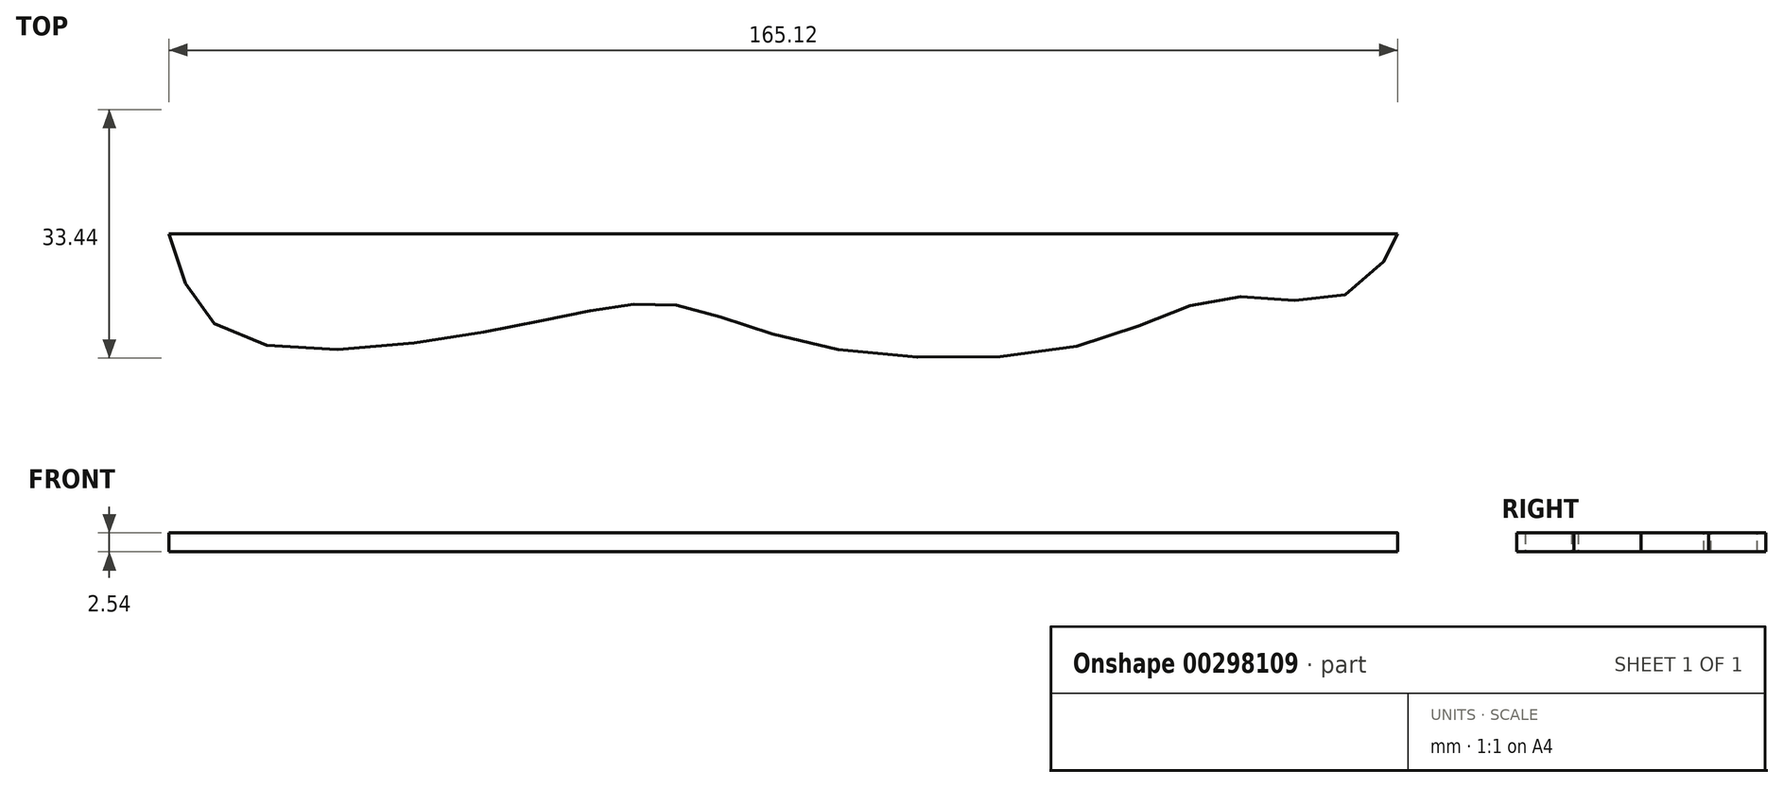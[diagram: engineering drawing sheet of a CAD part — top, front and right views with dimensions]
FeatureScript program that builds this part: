
annotation { "Feature Type Name" : "Feature", "Feature Type Description" : "" }
export const myFeature = defineFeature(function(context is Context, id is Id, definition is map)
    precondition{}
    {
        {
            var Q0;
            Q0=qCreatedBy(makeId("Top.planeOp"),FACE);
            var sketch = newSketch(context, id + "F0", { "sketchPlane" : qUnion([Q0])});
            skFitSpline(sketch, "E0", {"points": [v(-68.78, 0) * mm, v(-60.96, 13.19) * mm, v(-30.87, 13.97) * mm, v(-11.53, 10.26) * mm, v(0, 9.67) * mm, v(17, 14.75) * mm, v(54.7, 14.75) * mm, v(73.66, 8.5) * mm, v(90.27, 7.72) * mm, v(96.32, 0) * mm, v(95.93, 0) * mm], "startDerivative": vector(45.66, 160.82) * mm, "endDerivative": vector(-32.42, 11.33) * mm});
            skLineSegment(sketch, "E1", {"start": v(-68.78, 0) * mm, "end": v(96.32, 0) * mm});
            skSolve(sketch);
        }
        {
            var Q0;
            {var subQ0=sQuery(id+"F0.wireOp",EDGE,"E1");var subQ1=sQuery(id+"F0.wireOp",EDGE,"E0");var subQ2=makeQuery(id+"F0.imprint","INTERSECT",VERTEX,{"disambiguationData":[OD(0.0)],"derivedFrom":[subQ1,subQ0]});Q0=makeQuery(id+"F0.imprint","IMPRINT",FACE,{"disambiguationData":[TD([[makeQuery(id+"F0.imprint","IMPRINT",EDGE,{"disambiguationData":[TD([[subQ2,-1.0]])],"derivedFrom":subQ1}),-1.0]])]});}
            extrude(context, id + "F1", {"entities" : qUnion([Q0]), "depth" : 2.54 * mm});
        }
        {
            var Q0;
            Q0=makeQuery(id+"F1.opExtrude","SWEPT_BODY",BODY,{"disambiguationData":[OSD([sQuery(id+"F0.wireOp",EDGE,"E0"),sQuery(id+"F0.wireOp",EDGE,"E1")])]});
            transform(context, id + "F2", {"entities" : qUnion([Q0]), "transformType" : TransformType.TRANSLATION_3D, "dx" : 0 * mm, "dy" : 36.07 * mm, "dz" : 0 * mm, "makeCopy" : true});
        }
        {
            var Q0;
            Q0=makeQuery(id+"F2.opPattern","COPY",BODY,{"derivedFrom":makeQuery(id+"F1.opExtrude","SWEPT_BODY",BODY,{"disambiguationData":[OSD([sQuery(id+"F0.wireOp",EDGE,"E0"),sQuery(id+"F0.wireOp",EDGE,"E1")])]}),"instanceName":"1"});
            var Q1;
            Q1=makeQuery(id+"F2.opPattern","COPY",EDGE,{"derivedFrom":makeQuery(id+"F1.opExtrude","CAP_EDGE",EDGE,{"disambiguationData":[OSD([sQuery(id+"F0.wireOp",EDGE,"E1")])],"isStart":false}),"instanceName":"1"});
            transform(context, id + "F3", {"entities" : qUnion([Q0]), "transformType" : TransformType.ROTATION, "transformAxis" : qUnion([Q1]), "angle" : 180 * degree, "makeCopy" : false});
        }
        {
            var Q0;
            Q0=makeQuery(id+"F2.opPattern","COPY",BODY,{"derivedFrom":makeQuery(id+"F1.opExtrude","SWEPT_BODY",BODY,{"disambiguationData":[OSD([sQuery(id+"F0.wireOp",EDGE,"E0"),sQuery(id+"F0.wireOp",EDGE,"E1")])]}),"instanceName":"1"});
            transform(context, id + "F4", {"entities" : qUnion([Q0]), "transformType" : TransformType.TRANSLATION_3D, "dx" : 0 * mm, "dy" : -36.07 * mm, "dz" : 0 * mm, "makeCopy" : false});
        }
        {
            var Q0;
            Q0=makeQuery(id+"F2.opPattern","COPY",BODY,{"derivedFrom":makeQuery(id+"F1.opExtrude","SWEPT_BODY",BODY,{"disambiguationData":[OSD([sQuery(id+"F0.wireOp",EDGE,"E0"),sQuery(id+"F0.wireOp",EDGE,"E1")])]}),"instanceName":"1"});
            transform(context, id + "F5", {"entities" : qUnion([Q0]), "transformType" : TransformType.TRANSLATION_3D, "dx" : 0 * mm, "dy" : 0 * mm, "dz" : -2.54 * mm, "makeCopy" : false});
        }
    });
